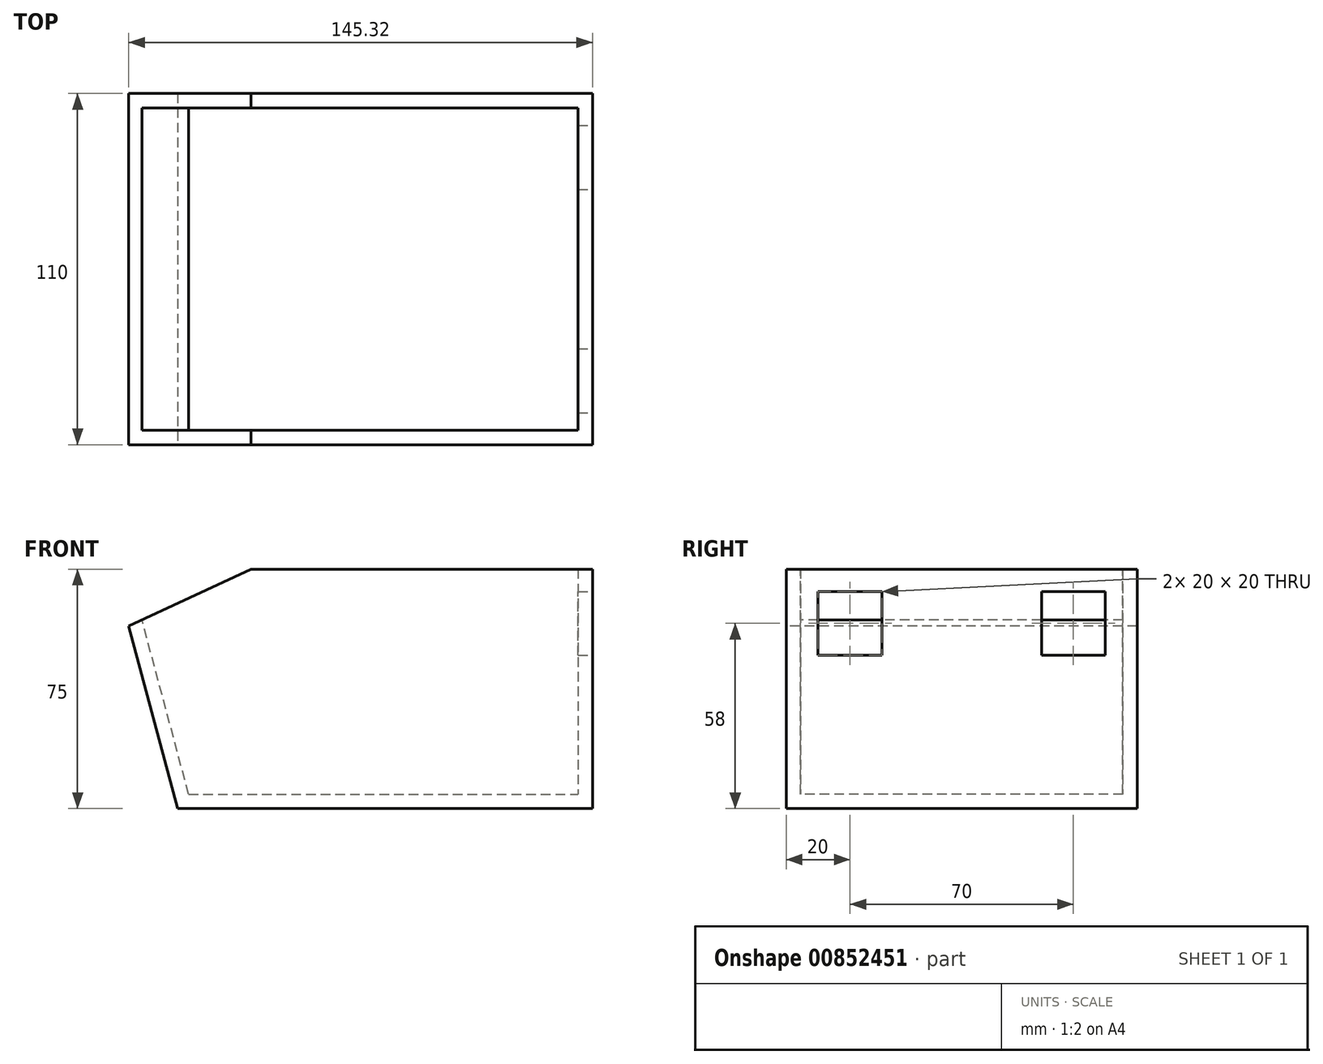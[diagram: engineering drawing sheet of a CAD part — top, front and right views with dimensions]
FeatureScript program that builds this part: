
annotation { "Feature Type Name" : "Feature", "Feature Type Description" : "" }
export const myFeature = defineFeature(function(context is Context, id is Id, definition is map)
    precondition{}
    {
        {
            var Q0;
            Q0=qCreatedBy(makeId("Top.planeOp"),FACE);
            var sketch = newSketch(context, id + "F0", { "sketchPlane" : qUnion([Q0])});
            skLineSegment(sketch, "E0.bottom", {"start": v(-65, 55) * mm, "end": v(65, 55) * mm});
            skLineSegment(sketch, "E0.top", {"start": v(-65, -55) * mm, "end": v(65, -55) * mm});
            skLineSegment(sketch, "E0.left", {"start": v(-65, 55) * mm, "end": v(-65, -55) * mm});
            skLineSegment(sketch, "E0.right", {"start": v(65, 55) * mm, "end": v(65, -55) * mm});
            skLineSegment(sketch, "E1", {"start": v(0, 0) * mm, "end": v(-110.28, 0) * mm, "construction": true});
            skLineSegment(sketch, "E2", {"start": v(0, 0) * mm, "end": v(0, 88.45) * mm, "construction": true});
            skSolve(sketch);
        }
        {
            var Q0;
            Q0=qSketchRegion(id+"F0",true);
            extrude(context, id + "F1", {"entities" : qUnion([Q0]), "depth" : 75 * mm});
        }
        {
            var Q0;
            Q0=makeQuery(id+"F1.opExtrude","SWEPT_FACE",FACE,{"disambiguationData":[OSD([sQuery(id+"F0.wireOp",EDGE,"E0.top")])]});
            var sketch = newSketch(context, id + "F2", { "sketchPlane" : qUnion([Q0])});
            skLineSegment(sketch, "E3", {"start": v(-65, 0) * mm, "end": v(-85.1, 75) * mm});
            skLineSegment(sketch, "E4", {"start": v(-85.1, 75) * mm, "end": v(-65, 75) * mm});
            skLineSegment(sketch, "E5", {"start": v(-65, 75) * mm, "end": v(-65, 0) * mm});
            skSolve(sketch);
        }
        {
            var Q0;
            Q0=qSketchRegion(id+"F2",true);
            var Q1;
            Q1=makeQuery(id+"F1.opExtrude","SWEPT_FACE",FACE,{"disambiguationData":[OSD([sQuery(id+"F0.wireOp",EDGE,"E0.bottom")])]});
            extrude(context, id + "F3", {"entities" : qUnion([Q0]), "operationType" : NewBodyOperationType.ADD, "endBound" : BoundingType.UP_TO_SURFACE, "oppositeDirection" : true, "endBoundEntityFace" : qUnion([Q1]), "depth" : 25 * mm});
        }
        {
            var Q0;
            Q0=makeQuery(id+"F3.boolean.opBoolean","MERGE",FACE,{"derivedFrom":[makeQuery(id+"F1.opExtrude","CAP_FACE",FACE,{"disambiguationData":[OSD([sQuery(id+"F0.wireOp",EDGE,"E0.bottom"),sQuery(id+"F0.wireOp",EDGE,"E0.top"),sQuery(id+"F0.wireOp",EDGE,"E0.left"),sQuery(id+"F0.wireOp",EDGE,"E0.right")])],"isStart":false}),makeQuery(id+"F3.opExtrude","SWEPT_FACE",FACE,{"disambiguationData":[OSD([sQuery(id+"F2.wireOp",EDGE,"E4")])]})]});
            shell(context, id + "F4", {"entities" : qUnion([Q0]), "thickness" : 4.5 * mm});
        }
        {
            var Q0;
            Q0=makeQuery(id+"F1.opExtrude","SWEPT_FACE",FACE,{"disambiguationData":[OSD([sQuery(id+"F0.wireOp",EDGE,"E0.top")])]});
            var sketch = newSketch(context, id + "F5", { "sketchPlane" : qUnion([Q0])});
            skLineSegment(sketch, "E6", {"start": v(-42.06, 75) * mm, "end": v(-80.32, 57.16) * mm});
            skLineSegment(sketch, "E7", {"start": v(-80.32, 57.16) * mm, "end": v(-85.42, 75) * mm});
            skLineSegment(sketch, "E8", {"start": v(-85.42, 75) * mm, "end": v(-42.06, 75) * mm});
            skSolve(sketch);
        }
        {
            var Q0;
            Q0=qSketchRegion(id+"F5",true);
            extrude(context, id + "F6", {"entities" : qUnion([Q0]), "operationType" : NewBodyOperationType.REMOVE, "endBound" : BoundingType.THROUGH_ALL, "oppositeDirection" : true, "depth" : 25 * mm});
        }
        {
            var Q0;
            Q0=makeQuery(id+"F1.opExtrude","SWEPT_FACE",FACE,{"disambiguationData":[OSD([sQuery(id+"F0.wireOp",EDGE,"E0.right")])]});
            var sketch = newSketch(context, id + "F7", { "sketchPlane" : qUnion([Q0])});
            skLineSegment(sketch, "E9.bottom", {"start": v(-45, 68) * mm, "end": v(-25, 68) * mm});
            skLineSegment(sketch, "E9.top", {"start": v(-45, 48) * mm, "end": v(-25, 48) * mm});
            skLineSegment(sketch, "E9.left", {"start": v(-45, 68) * mm, "end": v(-45, 48) * mm});
            skLineSegment(sketch, "E9.right", {"start": v(-25, 68) * mm, "end": v(-25, 48) * mm});
            skLineSegment(sketch, "E10", {"start": v(0, 0) * mm, "end": v(0, 84.79) * mm, "construction": true});
            skLineSegment(sketch, "E11.MirrorCS", {"start": v(45, 48) * mm, "end": v(25, 48) * mm});
            skLineSegment(sketch, "E12.MirrorCS", {"start": v(45, 68) * mm, "end": v(25, 68) * mm});
            skLineSegment(sketch, "E13.MirrorCS", {"start": v(25, 68) * mm, "end": v(25, 48) * mm});
            skLineSegment(sketch, "E14.MirrorCS", {"start": v(45, 68) * mm, "end": v(45, 48) * mm});
            skSolve(sketch);
        }
        {
            var Q0;
            Q0=qSketchRegion(id+"F7",true);
            extrude(context, id + "F8", {"entities" : qUnion([Q0]), "operationType" : NewBodyOperationType.REMOVE, "endBound" : BoundingType.UP_TO_NEXT, "oppositeDirection" : true, "depth" : 25 * mm});
        }
    });
